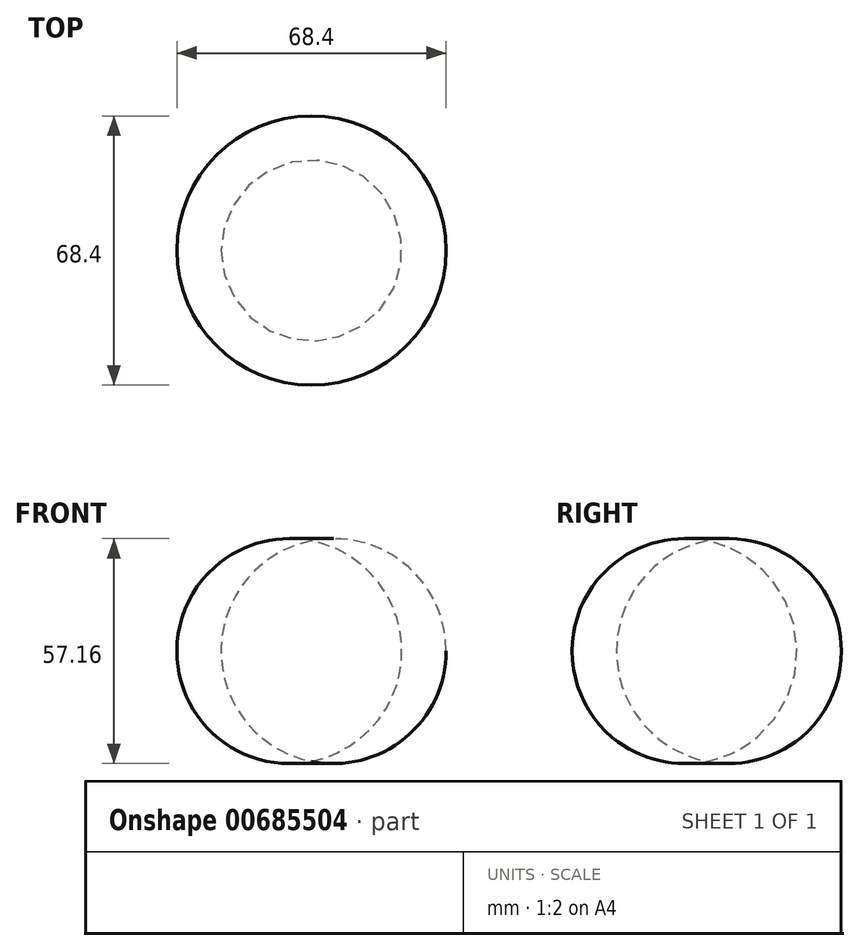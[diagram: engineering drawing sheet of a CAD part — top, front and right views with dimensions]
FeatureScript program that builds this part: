
annotation { "Feature Type Name" : "Feature", "Feature Type Description" : "" }
export const myFeature = defineFeature(function(context is Context, id is Id, definition is map)
    precondition{}
    {
        {
            var Q0;
            Q0=qCreatedBy(makeId("Front.planeOp"),FACE);
            var sketch = newSketch(context, id + "F0", { "sketchPlane" : qUnion([Q0])});
            skArc(sketch, "E0", {"start": v(0, 56.05) * mm, "mid": v(-22.96, 28.02) * mm, "end": v(0, 0) * mm});
            skLineSegment(sketch, "E1", {"start": v(0, 56.05) * mm, "end": v(0, 0) * mm});
            skSolve(sketch);
        }
        {
            var Q0;
            Q0 = qSketchRegion(id + "F0", true);
            var Q1;
            Q1=sQuery(id+"F0.wireOp",EDGE,"E1");
            revolve(context, id + "F1", {"entities" : qUnion([Q0]), "axis" : qUnion([Q1]), "revolveType" : RevolveType.FULL});
        }
    });
